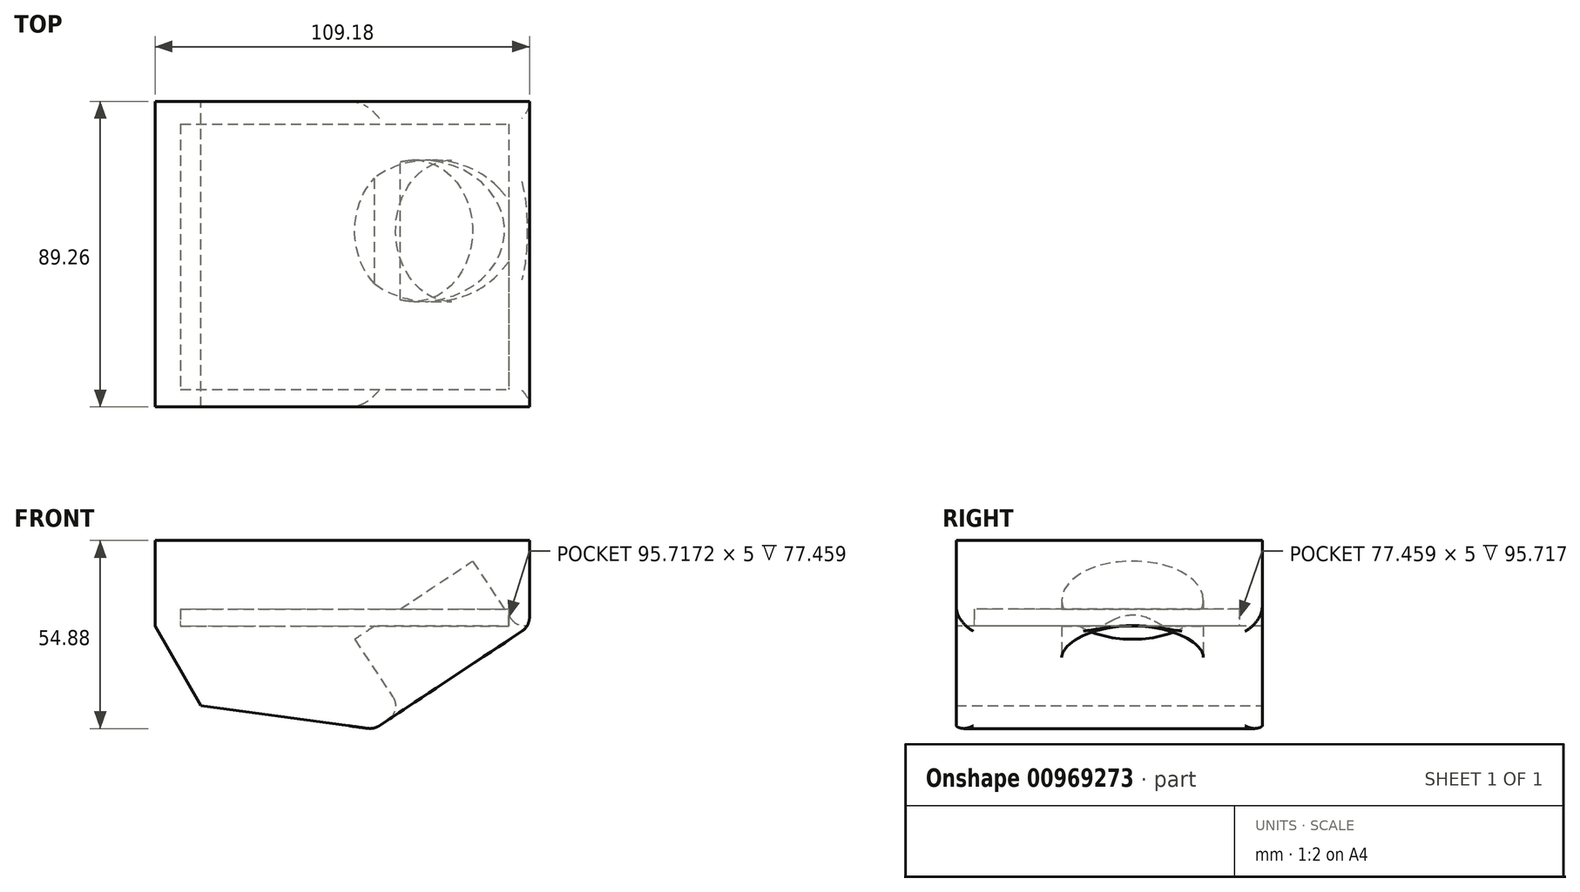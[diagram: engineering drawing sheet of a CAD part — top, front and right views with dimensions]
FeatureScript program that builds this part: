
annotation { "Feature Type Name" : "Feature", "Feature Type Description" : "" }
export const myFeature = defineFeature(function(context is Context, id is Id, definition is map)
    precondition{}
    {
        {
            var Q0;
            Q0=qCreatedBy(makeId("Top.planeOp"),FACE);
            var sketch = newSketch(context, id + "F0", { "sketchPlane" : qUnion([Q0])});
            skLineSegment(sketch, "E0.bottom", {"start": v(-48.23, 35.32) * mm, "end": v(60.95, 35.32) * mm});
            skLineSegment(sketch, "E0.top", {"start": v(-48.23, -53.94) * mm, "end": v(60.95, -53.94) * mm});
            skLineSegment(sketch, "E0.left", {"start": v(-48.23, 35.32) * mm, "end": v(-48.23, -53.94) * mm});
            skLineSegment(sketch, "E0.right", {"start": v(60.95, 35.32) * mm, "end": v(60.95, -53.94) * mm});
            skLineSegment(sketch, "E1.bottom", {"start": v(-40.85, 28.68) * mm, "end": v(54.87, 28.68) * mm});
            skLineSegment(sketch, "E1.top", {"start": v(-40.85, -48.78) * mm, "end": v(54.87, -48.78) * mm});
            skLineSegment(sketch, "E1.left", {"start": v(-40.85, 28.68) * mm, "end": v(-40.85, -48.78) * mm});
            skLineSegment(sketch, "E1.right", {"start": v(54.87, 28.68) * mm, "end": v(54.87, -48.78) * mm});
            skSolve(sketch);
        }
        {
            var Q0;
            Q0=makeQuery(id+"F0.imprint","IMPRINT",FACE,{"disambiguationData":[TD([[makeQuery(id+"F0.imprint","IMPRINT",EDGE,{"derivedFrom":sQuery(id+"F0.wireOp",EDGE,"E0.bottom")}),-1.0]])]});
            var Q1;
            Q1=makeQuery(id+"F0.imprint","IMPRINT",FACE,{"disambiguationData":[TD([[makeQuery(id+"F0.imprint","IMPRINT",EDGE,{"derivedFrom":sQuery(id+"F0.wireOp",EDGE,"E1.bottom")}),-1.0]])]});
            extrude(context, id + "F1", {"entities" : qUnion([Q0, Q1]), "depth" : 25 * mm, "offsetDistance" : 25 * mm});
        }
        {
            var Q0;
            Q0=makeQuery(id+"F0.imprint","IMPRINT",FACE,{"disambiguationData":[TD([[makeQuery(id+"F0.imprint","IMPRINT",EDGE,{"derivedFrom":sQuery(id+"F0.wireOp",EDGE,"E1.bottom")}),-1.0]])]});
            extrude(context, id + "F2", {"entities" : qUnion([Q0]), "operationType" : NewBodyOperationType.REMOVE, "depth" : 5 * mm, "offsetDistance" : 25 * mm});
        }
        {
            var Q0;
            Q0=makeQuery(id+"F1.opExtrude","SWEPT_FACE",FACE,{"disambiguationData":[OSD([sQuery(id+"F0.wireOp",EDGE,"E0.bottom")])]});
            var sketch = newSketch(context, id + "F3", { "sketchPlane" : qUnion([Q0])});
            skLineSegment(sketch, "E2", {"start": v(-60.95, 0) * mm, "end": v(-15.61, -30.08) * mm});
            skLineSegment(sketch, "E3", {"start": v(-15.61, -30.08) * mm, "end": v(34.95, -23.26) * mm});
            skLineSegment(sketch, "E4", {"start": v(34.95, -23.26) * mm, "end": v(48.23, 0) * mm});
            skLineSegment(sketch, "E5", {"start": v(48.23, 0) * mm, "end": v(-60.95, 0) * mm});
            skSolve(sketch);
        }
        {
            var Q0;
            Q0=makeQuery(id+"F3.imprint","IMPRINT",FACE,{"disambiguationData":[TD([[makeQuery(id+"F3.imprint","IMPRINT",EDGE,{"derivedFrom":sQuery(id+"F3.wireOp",EDGE,"E2")}),1.0]])]});
            var Q1;
            Q1=makeQuery(id+"F1.opExtrude","SWEPT_FACE",FACE,{"disambiguationData":[OSD([sQuery(id+"F0.wireOp",EDGE,"E0.top")])]});
            extrude(context, id + "F4", {"entities" : qUnion([Q0]), "operationType" : NewBodyOperationType.ADD, "endBound" : BoundingType.UP_TO_SURFACE, "oppositeDirection" : true, "depth" : 25 * mm, "endBoundEntityFace" : qUnion([Q1]), "offsetDistance" : 25 * mm});
        }
        {
            var Q0;
            Q0=makeQuery(id+"F4.opExtrude","SWEPT_FACE",FACE,{"disambiguationData":[OSD([sQuery(id+"F3.wireOp",EDGE,"E2")])]});
            var sketch = newSketch(context, id + "F5", { "sketchPlane" : qUnion([Q0])});
            skCircle(sketch, "E6", {"center": v(26.84, 2.51) * mm, "radius": 20.65 * mm});
            skSolve(sketch);
        }
        {
            var Q0;
            Q0=makeQuery(id+"F5.imprint","IMPRINT",FACE,{"disambiguationData":[TD([[makeQuery(id+"F5.imprint","IMPRINT",EDGE,{"derivedFrom":sQuery(id+"F5.wireOp",EDGE,"E6")}),1.0]])]});
            extrude(context, id + "F6", {"entities" : qUnion([Q0]), "operationType" : NewBodyOperationType.REMOVE, "oppositeDirection" : true, "depth" : 25 * mm, "offsetDistance" : 25 * mm});
        }
        {
            var Q0;
            Q0=makeQuery(id+"F4.opExtrude","SWEPT_FACE",FACE,{"disambiguationData":[OSD([sQuery(id+"F3.wireOp",EDGE,"E2")])]});
            fillet(context, id + "F7", {"entities" : qUnion([Q0]), "tangentPropagation" : true, "radius" : 5 * mm, "defaultsChanged" : false, "vertexSettings" : [], "allowEdgeOverflow" : false});
        }
    });
